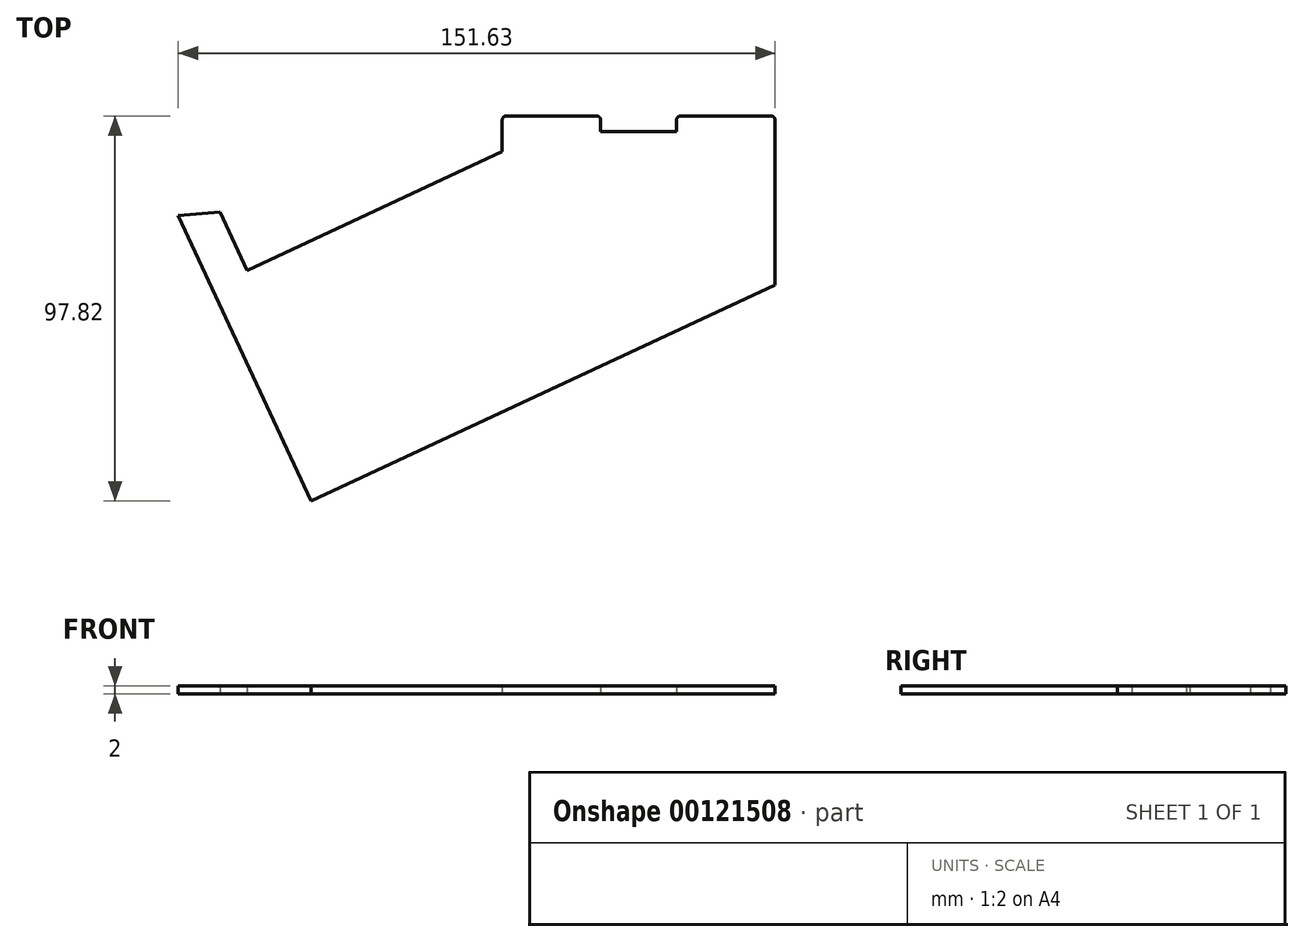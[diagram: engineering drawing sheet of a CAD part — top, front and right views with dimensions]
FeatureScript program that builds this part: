
annotation { "Feature Type Name" : "Feature", "Feature Type Description" : "" }
export const myFeature = defineFeature(function(context is Context, id is Id, definition is map)
    precondition{}
    {
        {
            var Q0;
            Q0=qCreatedBy(makeId("Top.planeOp"),FACE);
            var sketch = newSketch(context, id + "F0", { "sketchPlane" : qUnion([Q0])});
            skLineSegment(sketch, "E0", {"start": v(62.1, 50.85) * mm, "end": v(62.1, 46.85) * mm});
            skLineSegment(sketch, "E1", {"start": v(62.1, 46.85) * mm, "end": v(62.1, 7.97) * mm});
            skLineSegment(sketch, "E2", {"start": v(62.1, 50.85) * mm, "end": v(37.1, 50.85) * mm});
            skLineSegment(sketch, "E3", {"start": v(37.1, 50.85) * mm, "end": v(37.1, 46.85) * mm});
            skLineSegment(sketch, "E4", {"start": v(37.1, 46.85) * mm, "end": v(17.8, 46.85) * mm});
            skLineSegment(sketch, "E5", {"start": v(17.8, 46.85) * mm, "end": v(17.8, 50.85) * mm});
            skLineSegment(sketch, "E6", {"start": v(17.8, 50.85) * mm, "end": v(-7.2, 50.85) * mm});
            skLineSegment(sketch, "E7", {"start": v(-7.2, 50.85) * mm, "end": v(-7.2, 46.85) * mm});
            skLineSegment(sketch, "E8", {"start": v(-7.2, 46.85) * mm, "end": v(-7.2, 41.85) * mm});
            skLineSegment(sketch, "E9", {"start": v(-7.2, 41.85) * mm, "end": v(-72.02, 11.63) * mm});
            skLineSegment(sketch, "E10", {"start": v(-89.53, 25.53) * mm, "end": v(-55.72, -46.97) * mm});
            skLineSegment(sketch, "E11", {"start": v(-55.72, -46.97) * mm, "end": v(62.1, 7.97) * mm});
            skLineSegment(sketch, "E12", {"start": v(-89.53, 25.53) * mm, "end": v(-78.93, 26.46) * mm});
            skLineSegment(sketch, "E13", {"start": v(-78.93, 26.46) * mm, "end": v(-72.02, 11.63) * mm});
            skSolve(sketch);
        }
        {
            var Q0;
            Q0=makeQuery(id+"F0.imprint","IMPRINT",FACE,{"disambiguationData":[TD([[makeQuery(id+"F0.imprint","IMPRINT",EDGE,{"derivedFrom":sQuery(id+"F0.wireOp",EDGE,"E0")}),-1.0]])]});
            extrude(context, id + "F1", {"entities" : qUnion([Q0]), "depth" : 2 * mm});
        }
        {
            var Q0;
            Q0=makeQuery(id+"F1.opExtrude","SWEPT_EDGE",EDGE,{"disambiguationData":[OSD([sQuery(id+"F0.wireOp",EDGE,"E2"),sQuery(id+"F0.wireOp",EDGE,"E3")])]});
            var Q1;
            Q1=makeQuery(id+"F1.opExtrude","SWEPT_EDGE",EDGE,{"disambiguationData":[OSD([sQuery(id+"F0.wireOp",EDGE,"E0"),sQuery(id+"F0.wireOp",EDGE,"E2")])]});
            var Q2;
            Q2=makeQuery(id+"F1.opExtrude","SWEPT_EDGE",EDGE,{"disambiguationData":[OSD([sQuery(id+"F0.wireOp",EDGE,"E5"),sQuery(id+"F0.wireOp",EDGE,"E6")])]});
            var Q3;
            Q3=makeQuery(id+"F1.opExtrude","SWEPT_EDGE",EDGE,{"disambiguationData":[OSD([sQuery(id+"F0.wireOp",EDGE,"E6"),sQuery(id+"F0.wireOp",EDGE,"E7")])]});
            fillet(context, id + "F2", {"entities" : qUnion([Q0, Q1, Q2, Q3]), "radius" : 1 * mm, "tangentPropagation" : true, "allowEdgeOverflow" : false});
        }
    });
